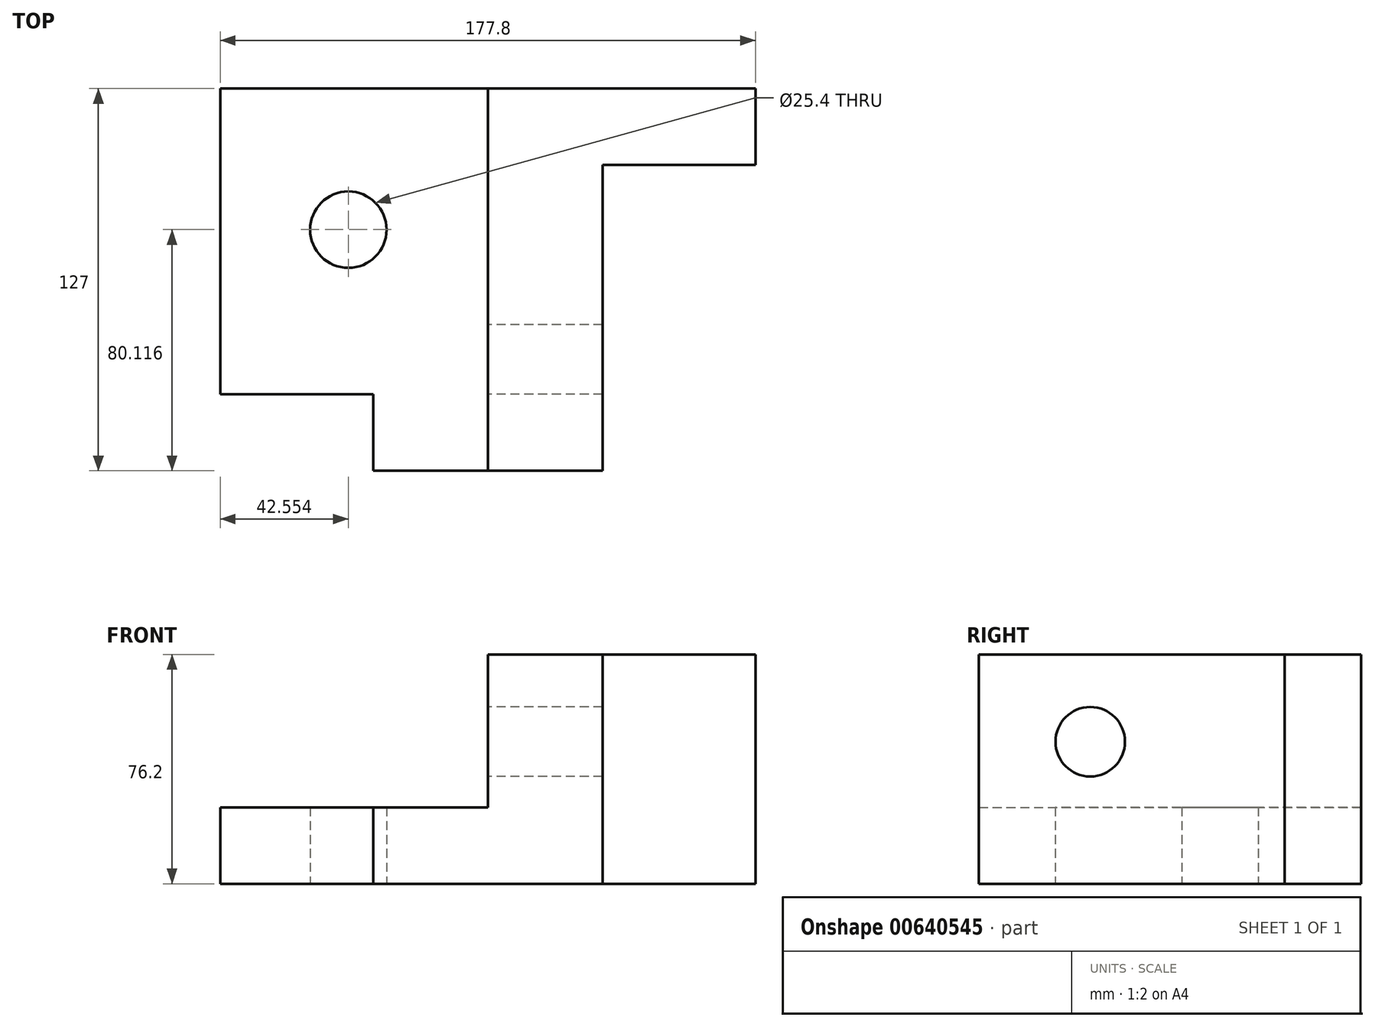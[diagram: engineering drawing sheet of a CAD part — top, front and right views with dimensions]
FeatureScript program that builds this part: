
annotation { "Feature Type Name" : "Feature", "Feature Type Description" : "" }
export const myFeature = defineFeature(function(context is Context, id is Id, definition is map)
    precondition{}
    {
        {
            var Q0;
            Q0=qCreatedBy(makeId("Top.planeOp"),FACE);
            var sketch = newSketch(context, id + "F0", { "sketchPlane" : qUnion([Q0])});
            skLineSegment(sketch, "E0.bottom", {"start": v(88.9, 63.5) * mm, "end": v(-88.9, 63.5) * mm});
            skLineSegment(sketch, "E0.top", {"start": v(38.1, -63.5) * mm, "end": v(-38.1, -63.5) * mm});
            skLineSegment(sketch, "E0.left", {"start": v(88.9, 63.5) * mm, "end": v(88.9, 38.1) * mm});
            skLineSegment(sketch, "E0.right", {"start": v(-88.9, 63.5) * mm, "end": v(-88.9, -38.1) * mm});
            skPoint(sketch, "E0.middle", {"position": v(0, 0) * mm});
            skLineSegment(sketch, "E1", {"start": v(-38.1, -63.5) * mm, "end": v(-38.1, -38.1) * mm});
            skLineSegment(sketch, "E2", {"start": v(-38.1, -38.1) * mm, "end": v(-88.9, -38.1) * mm});
            skPoint(sketch, "E3.orphan", {"position": v(-88.9, -63.5) * mm});
            skLineSegment(sketch, "E4", {"start": v(38.1, -63.5) * mm, "end": v(38.1, 38.1) * mm});
            skLineSegment(sketch, "E5", {"start": v(38.1, 38.1) * mm, "end": v(88.9, 38.1) * mm});
            skPoint(sketch, "E6.orphan", {"position": v(88.9, -63.5) * mm});
            skLineSegment(sketch, "E7", {"start": v(-38.1, -63.5) * mm, "end": v(0, -63.5) * mm});
            skLineSegment(sketch, "E8", {"start": v(0, -63.5) * mm, "end": v(0, 63.5) * mm});
            skCircle(sketch, "E9", {"center": v(-46.35, 16.62) * mm, "radius": 12.7 * mm});
            skSolve(sketch);
        }
        {
            var Q0;
            {var subQ0=sQuery(id+"F0.wireOp",EDGE,"E0.right");Q0=makeQuery(id+"F0.imprint","IMPRINT",FACE,{"disambiguationData":[TD([[makeQuery(id+"F0.imprint","IMPRINT",EDGE,{"derivedFrom":subQ0}),1.0]])]});}
            extrude(context, id + "F1", {"entities" : qUnion([Q0]), "depth" : 25.4 * mm, "offsetDistance" : 25.4 * mm});
        }
        {
            var Q0;
            Q0=makeQuery(id+"F0.imprint","IMPRINT",FACE,{"disambiguationData":[TD([[makeQuery(id+"F0.imprint","IMPRINT",EDGE,{"derivedFrom":sQuery(id+"F0.wireOp",EDGE,"E0.top")}),-1.0]])]});
            extrude(context, id + "F2", {"entities" : qUnion([Q0]), "operationType" : NewBodyOperationType.ADD, "depth" : 76.2 * mm, "offsetDistance" : 25.4 * mm});
        }
        {
            var Q0;
            Q0=qCreatedBy(makeId("Right.planeOp"),FACE);
            var sketch = newSketch(context, id + "F3", { "sketchPlane" : qUnion([Q0])});
            skCircle(sketch, "E10", {"center": v(-26.47, 47.17) * mm, "radius": 11.54 * mm});
            skSolve(sketch);
        }
        {
            var Q0;
            Q0 = qSketchRegion(id + "F3", true);
            extrude(context, id + "F4", {"entities" : qUnion([Q0]), "operationType" : NewBodyOperationType.REMOVE, "depth" : 97.03 * mm, "offsetDistance" : 25.4 * mm});
        }
    });
